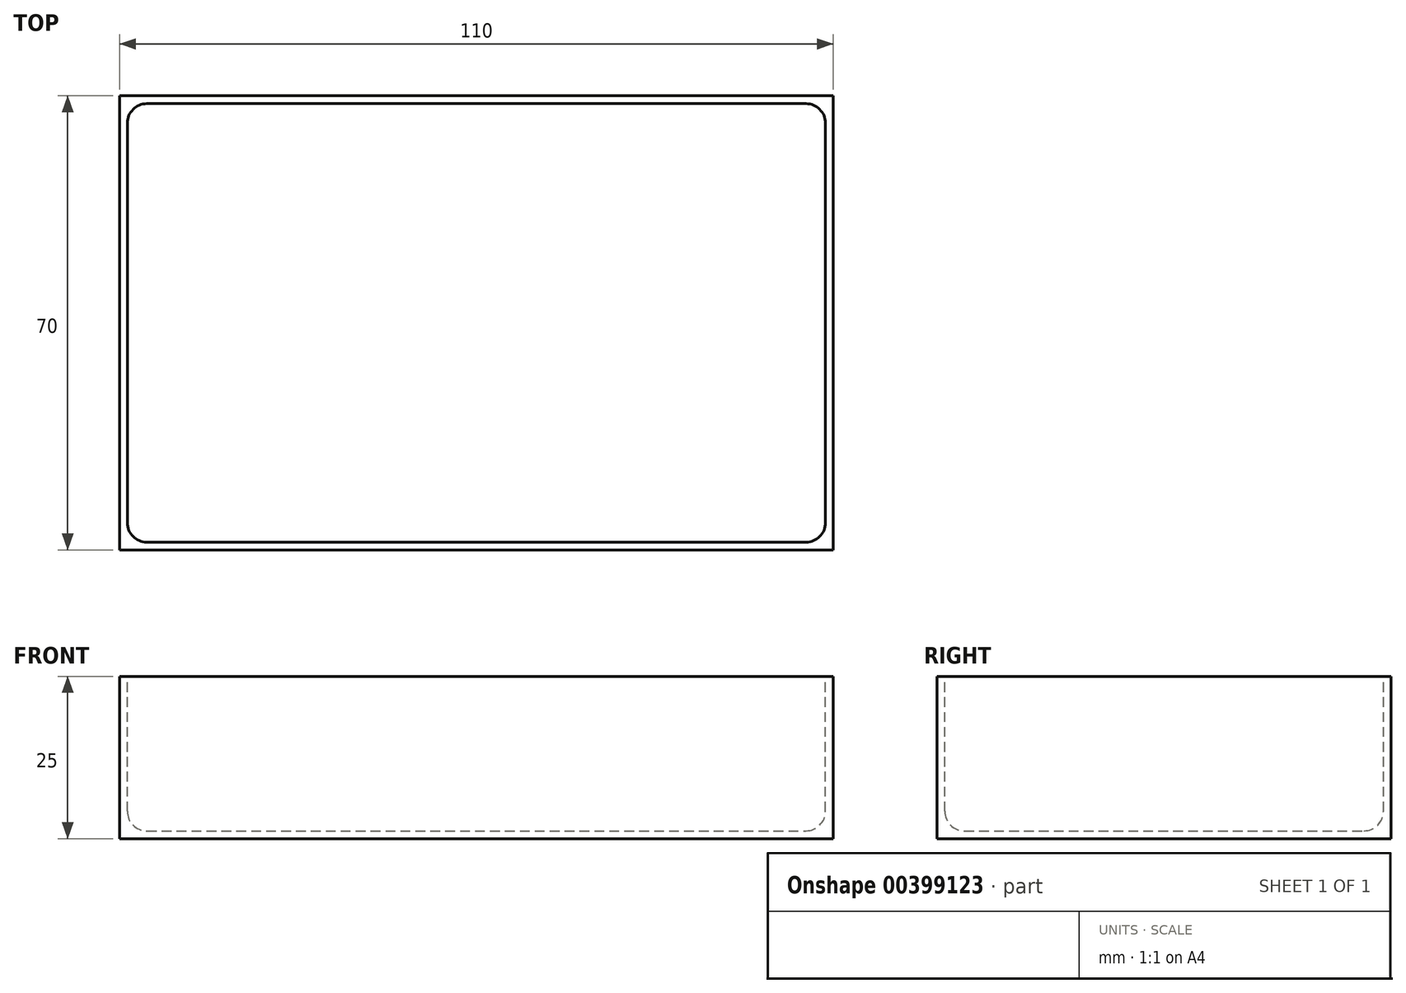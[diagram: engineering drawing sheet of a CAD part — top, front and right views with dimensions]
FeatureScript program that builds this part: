
annotation { "Feature Type Name" : "Feature", "Feature Type Description" : "" }
export const myFeature = defineFeature(function(context is Context, id is Id, definition is map)
    precondition{}
    {
        {
            var Q0;
            Q0=qCreatedBy(makeId("Top.planeOp"),FACE);
            var sketch = newSketch(context, id + "F0", { "sketchPlane" : qUnion([Q0])});
            skLineSegment(sketch, "E0.bottom", {"start": v(-55, -35) * mm, "end": v(55, -35) * mm});
            skLineSegment(sketch, "E0.top", {"start": v(-55, 35) * mm, "end": v(55, 35) * mm});
            skLineSegment(sketch, "E0.left", {"start": v(-55, -35) * mm, "end": v(-55, 35) * mm});
            skLineSegment(sketch, "E0.right", {"start": v(55, -35) * mm, "end": v(55, 35) * mm});
            skPoint(sketch, "E0.middle", {"position": v(0, 0) * mm});
            skSolve(sketch);
        }
        {
            var Q0;
            Q0 = qSketchRegion(id + "F0", true);
            extrude(context, id + "F1", {"entities" : qUnion([Q0]), "depth" : 25 * mm});
        }
        {
            var Q0;
            Q0=makeQuery(id+"F1.opExtrude","CAP_FACE",FACE,{"disambiguationData":[OSD([sQuery(id+"F0.wireOp",EDGE,"E0.bottom"),sQuery(id+"F0.wireOp",EDGE,"E0.top"),sQuery(id+"F0.wireOp",EDGE,"E0.left"),sQuery(id+"F0.wireOp",EDGE,"E0.right")])],"isStart":false});
            var sketch = newSketch(context, id + "F2", { "sketchPlane" : qUnion([Q0])});
            skLineSegment(sketch, "E1.bottom", {"start": v(-53.8, -33.8) * mm, "end": v(53.8, -33.8) * mm});
            skLineSegment(sketch, "E1.top", {"start": v(-53.8, 33.8) * mm, "end": v(53.8, 33.8) * mm});
            skLineSegment(sketch, "E1.left", {"start": v(-53.8, -33.8) * mm, "end": v(-53.8, 33.8) * mm});
            skLineSegment(sketch, "E1.right", {"start": v(53.8, -33.8) * mm, "end": v(53.8, 33.8) * mm});
            skPoint(sketch, "E1.middle", {"position": v(0, 0) * mm});
            skSolve(sketch);
        }
        {
            var Q0;
            Q0 = qSketchRegion(id + "F2", true);
            extrude(context, id + "F3", {"entities" : qUnion([Q0]), "operationType" : NewBodyOperationType.REMOVE, "oppositeDirection" : true, "depth" : 23.8 * mm});
        }
        {
            var Q0;
            Q0=makeQuery(id+"F3.boolean.opBoolean","COPY",EDGE,{"derivedFrom":makeQuery(id+"F3.opExtrude","SWEPT_EDGE",EDGE,{"disambiguationData":[OSD([sQuery(id+"F2.wireOp",EDGE,"E1.top"),sQuery(id+"F2.wireOp",EDGE,"E1.left")])]})});
            var Q1;
            Q1=makeQuery(id+"F3.boolean.opBoolean","COPY",EDGE,{"derivedFrom":makeQuery(id+"F3.opExtrude","CAP_EDGE",EDGE,{"disambiguationData":[OSD([sQuery(id+"F2.wireOp",EDGE,"E1.left")])],"isStart":false})});
            var Q2;
            Q2=makeQuery(id+"F3.boolean.opBoolean","COPY",EDGE,{"derivedFrom":makeQuery(id+"F3.opExtrude","CAP_EDGE",EDGE,{"disambiguationData":[OSD([sQuery(id+"F2.wireOp",EDGE,"E1.top")])],"isStart":false})});
            var Q3;
            Q3=makeQuery(id+"F3.boolean.opBoolean","COPY",EDGE,{"derivedFrom":makeQuery(id+"F3.opExtrude","SWEPT_EDGE",EDGE,{"disambiguationData":[OSD([sQuery(id+"F2.wireOp",EDGE,"E1.top"),sQuery(id+"F2.wireOp",EDGE,"E1.right")])]})});
            var Q4;
            Q4=makeQuery(id+"F3.boolean.opBoolean","COPY",EDGE,{"derivedFrom":makeQuery(id+"F3.opExtrude","CAP_EDGE",EDGE,{"disambiguationData":[OSD([sQuery(id+"F2.wireOp",EDGE,"E1.right")])],"isStart":false})});
            var Q5;
            Q5=makeQuery(id+"F3.boolean.opBoolean","COPY",EDGE,{"derivedFrom":makeQuery(id+"F3.opExtrude","SWEPT_EDGE",EDGE,{"disambiguationData":[OSD([sQuery(id+"F2.wireOp",EDGE,"E1.bottom"),sQuery(id+"F2.wireOp",EDGE,"E1.right")])]})});
            var Q6;
            Q6=makeQuery(id+"F3.boolean.opBoolean","COPY",EDGE,{"derivedFrom":makeQuery(id+"F3.opExtrude","CAP_EDGE",EDGE,{"disambiguationData":[OSD([sQuery(id+"F2.wireOp",EDGE,"E1.bottom")])],"isStart":false})});
            var Q7;
            Q7=makeQuery(id+"F3.boolean.opBoolean","COPY",EDGE,{"derivedFrom":makeQuery(id+"F3.opExtrude","SWEPT_EDGE",EDGE,{"disambiguationData":[OSD([sQuery(id+"F2.wireOp",EDGE,"E1.bottom"),sQuery(id+"F2.wireOp",EDGE,"E1.left")])]})});
            fillet(context, id + "F4", {"entities" : qUnion([Q0, Q1, Q2, Q3, Q4, Q5, Q6, Q7]), "radius" : 3 * mm, "tangentPropagation" : true, "allowEdgeOverflow" : false});
        }
    });
